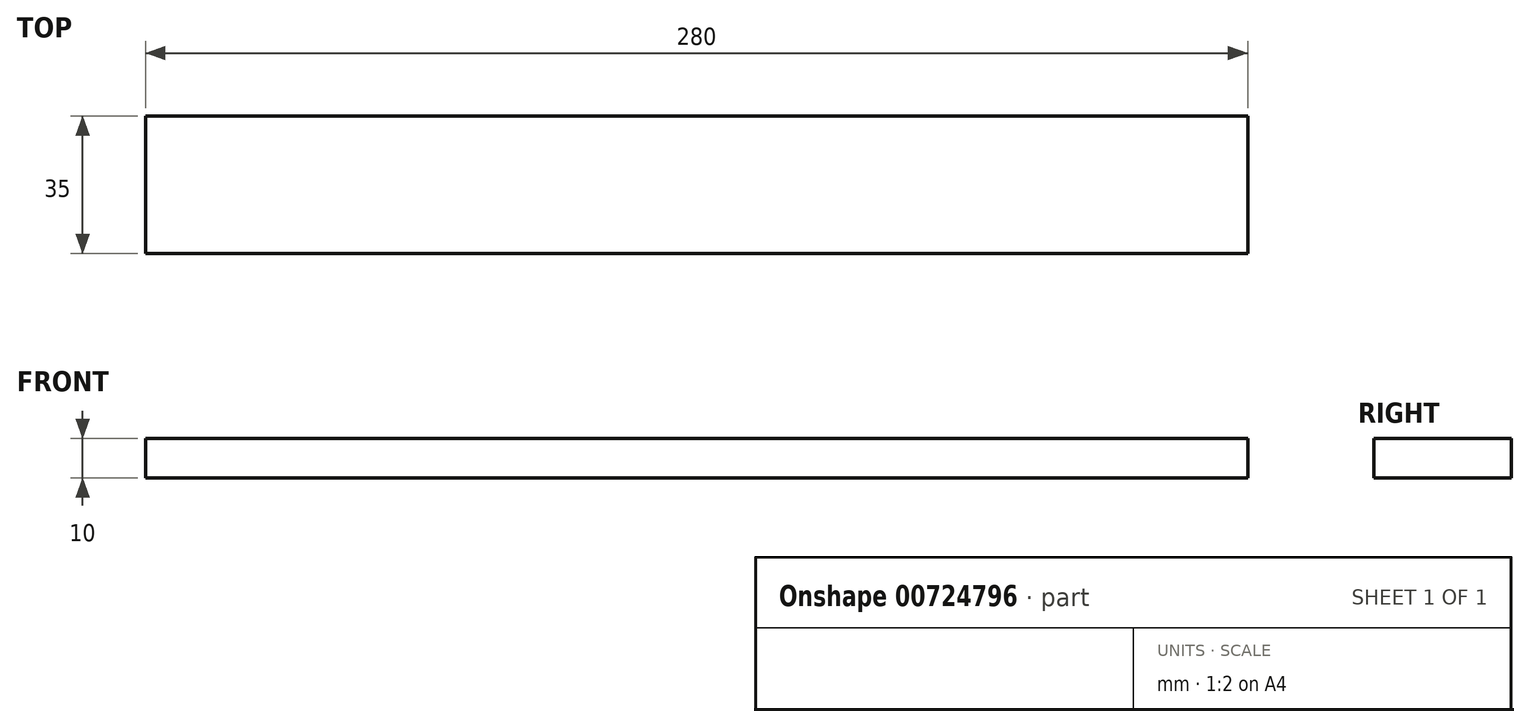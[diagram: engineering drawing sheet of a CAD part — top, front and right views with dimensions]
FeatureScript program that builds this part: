
annotation { "Feature Type Name" : "Feature", "Feature Type Description" : "" }
export const myFeature = defineFeature(function(context is Context, id is Id, definition is map)
    precondition{}
    {
        {
            var Q0;
            Q0=qCreatedBy(makeId("Right.planeOp"),FACE);
            var sketch = newSketch(context, id + "F0", { "sketchPlane" : qUnion([Q0])});
            skLineSegment(sketch, "E0.bottom", {"start": v(42.37, 0) * mm, "end": v(7.37, 0) * mm});
            skLineSegment(sketch, "E0.top", {"start": v(42.37, 10) * mm, "end": v(7.37, 10) * mm});
            skLineSegment(sketch, "E0.left", {"start": v(42.37, 0) * mm, "end": v(42.37, 10) * mm});
            skLineSegment(sketch, "E0.right", {"start": v(7.37, 0) * mm, "end": v(7.37, 10) * mm});
            skSolve(sketch);
        }
        {
            var Q0;
            Q0 = qSketchRegion(id + "F0", true);
            extrude(context, id + "F1", {"entities" : qUnion([Q0]), "depth" : 280 * mm, "offsetDistance" : 25 * mm});
        }
    });
